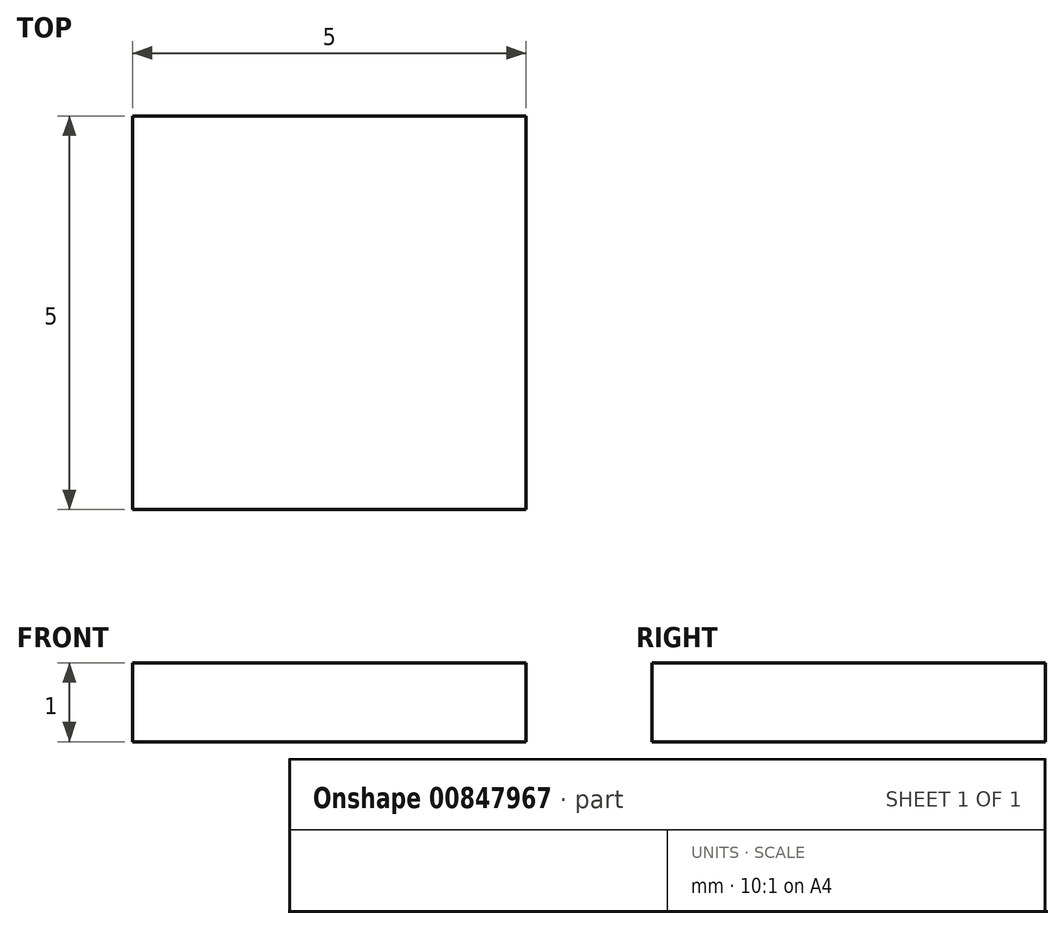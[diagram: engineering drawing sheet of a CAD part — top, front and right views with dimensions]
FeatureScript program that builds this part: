
annotation { "Feature Type Name" : "Feature", "Feature Type Description" : "" }
export const myFeature = defineFeature(function(context is Context, id is Id, definition is map)
    precondition{}
    {
        {
            var Q0;
            Q0=qCreatedBy(makeId("Top.planeOp"),FACE);
            var sketch = newSketch(context, id + "F0", { "sketchPlane" : qUnion([Q0])});
            skLineSegment(sketch, "E0.bottom", {"start": v(2.5, -2.5) * mm, "end": v(-2.5, -2.5) * mm});
            skLineSegment(sketch, "E0.top", {"start": v(2.5, 2.5) * mm, "end": v(-2.5, 2.5) * mm});
            skLineSegment(sketch, "E0.left", {"start": v(2.5, -2.5) * mm, "end": v(2.5, 2.5) * mm});
            skLineSegment(sketch, "E0.right", {"start": v(-2.5, -2.5) * mm, "end": v(-2.5, 2.5) * mm});
            skPoint(sketch, "E0.middle", {"position": v(0, 0) * mm});
            skSolve(sketch);
        }
        {
            var Q0;
            Q0 = qSketchRegion(id + "F0", true);
            extrude(context, id + "F1", {"entities" : qUnion([Q0]), "depth" : 1 * mm, "offsetDistance" : 25 * mm});
        }
    });
